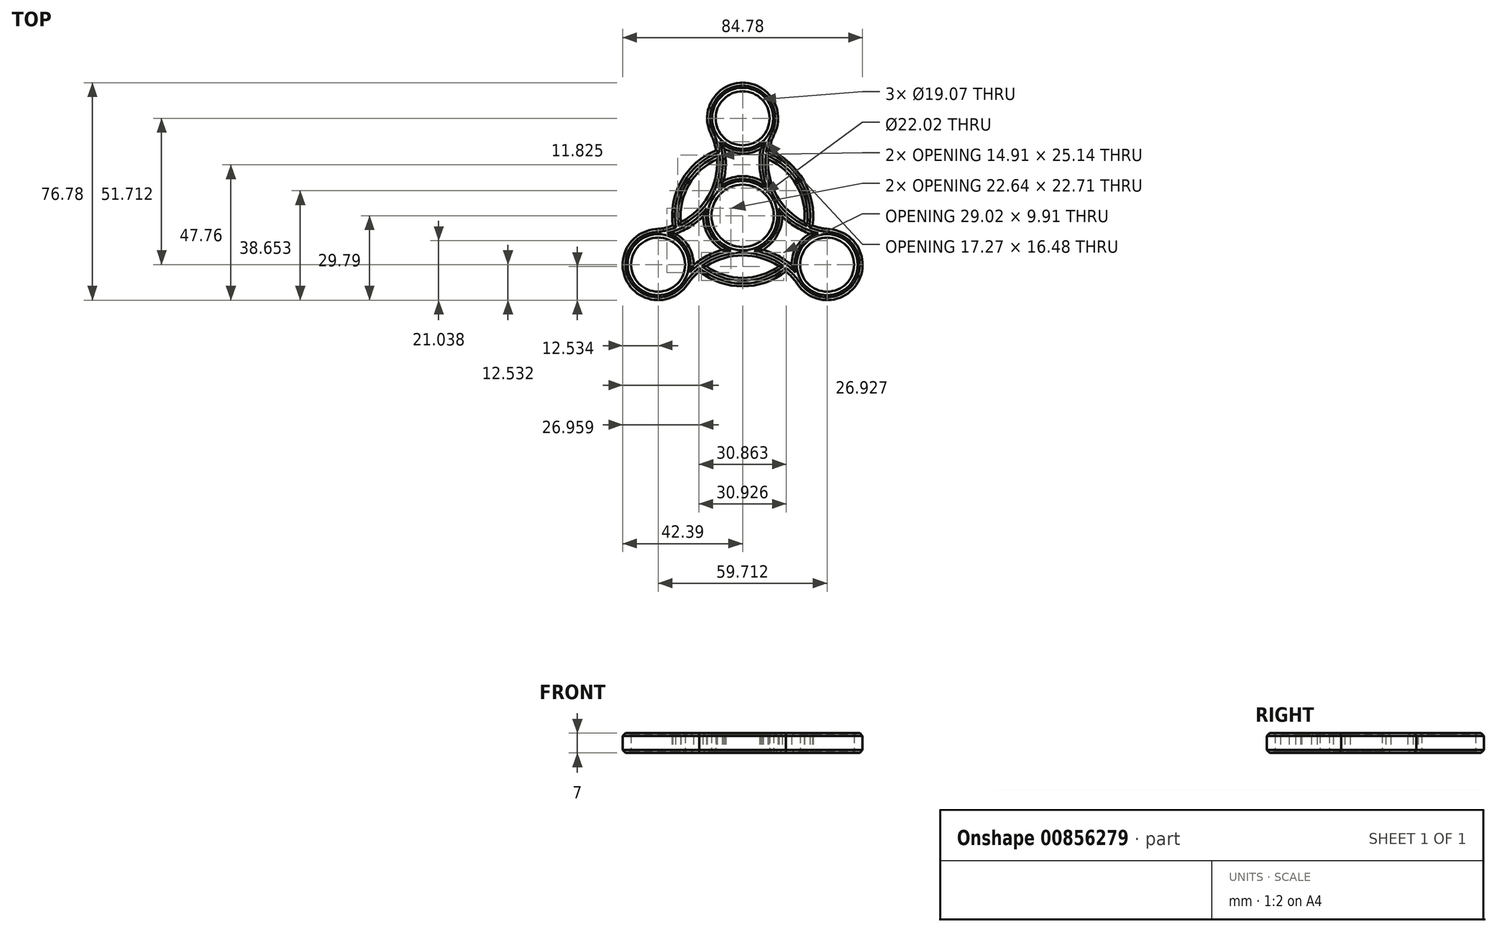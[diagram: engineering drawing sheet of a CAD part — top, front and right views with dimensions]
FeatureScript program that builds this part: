
annotation { "Feature Type Name" : "Feature", "Feature Type Description" : "" }
export const myFeature = defineFeature(function(context is Context, id is Id, definition is map)
    precondition{}
    {
        {
            var Q0;
            Q0=qCreatedBy(makeId("Top.planeOp"),FACE);
            var sketch = newSketch(context, id + "F0", { "sketchPlane" : qUnion([Q0])});
            skCircle(sketch, "E0", {"center": v(0, 0) * mm, "radius": 11.01 * mm});
            skCircle(sketch, "E1", {"center": v(0, 34.45) * mm, "radius": 9.54 * mm});
            skPoint(sketch, "E2", {"position": v(0, 43.99) * mm});
            skPoint(sketch, "E3", {"position": v(0, -11.01) * mm});
            skCircle(sketch, "E4.1.0", {"center": v(-29.86, -17.26) * mm, "radius": 9.54 * mm});
            skCircle(sketch, "E4.2.0", {"center": v(29.86, -17.26) * mm, "radius": 9.54 * mm});
            skPoint(sketch, "E4.center", {"position": v(0, -0.02) * mm});
            skArc(sketch, "E5", {"start": v(6.43, 23.7) * mm, "mid": v(5.99, 17.95) * mm, "end": v(6.8, 12.25) * mm});
            skArc(sketch, "E6", {"start": v(-23.75, -6.31) * mm, "mid": v(-18.55, -3.81) * mm, "end": v(-14, -0.25) * mm});
            skArc(sketch, "E7", {"start": v(17.32, -17.42) * mm, "mid": v(12.57, -14.17) * mm, "end": v(7.22, -12) * mm});
            skPoint(sketch, "E8", {"position": v(-21.98, -22.63) * mm});
            skPoint(sketch, "E9", {"position": v(-30.58, -7.75) * mm});
            skPoint(sketch, "E10", {"position": v(-8.6, 30.33) * mm});
            skPoint(sketch, "E11", {"position": v(8.6, 30.33) * mm});
            skPoint(sketch, "E12", {"position": v(30.58, -7.75) * mm});
            skPoint(sketch, "E13", {"position": v(21.98, -22.63) * mm});
            skPoint(sketch, "E14", {"position": v(-39.4, -17.26) * mm});
            skArc(sketch, "E15.0", {"start": v(-30.81, -4.76) * mm, "mid": v(-27.7, -4.31) * mm, "end": v(-24.68, -3.46) * mm});
            skArc(sketch, "E16.0", {"start": v(11.3, 29.03) * mm, "mid": v(10.14, 26.13) * mm, "end": v(9.37, 23.1) * mm});
            skArc(sketch, "E17.0", {"start": v(19.5, -24.32) * mm, "mid": v(17.56, -21.85) * mm, "end": v(15.32, -19.66) * mm});
            skArc(sketch, "E18.0", {"start": v(-17.32, -17.42) * mm, "mid": v(-19, -10.98) * mm, "end": v(-23.75, -6.31) * mm});
            skLineSegment(sketch, "E19.0", {"start": v(0, 46.99) * mm, "end": v(0, 46.99) * mm});
            skArc(sketch, "E20.0", {"start": v(23.75, -6.31) * mm, "mid": v(19, -10.98) * mm, "end": v(17.32, -17.42) * mm});
            skArc(sketch, "E21.0", {"start": v(6.8, 12.25) * mm, "mid": v(0, 14.01) * mm, "end": v(-6.8, 12.25) * mm});
            skArc(sketch, "E22.trimOffspring", {"start": v(0, 46.99) * mm, "mid": v(-10.6, 41.13) * mm, "end": v(-11.3, 29.03) * mm});
            skArc(sketch, "E23.trimOffspring", {"start": v(-6.43, 23.7) * mm, "mid": v(0, 21.92) * mm, "end": v(6.43, 23.7) * mm});
            skArc(sketch, "E24.trimOffspring", {"start": v(11.3, 29.03) * mm, "mid": v(11.3, 29.04) * mm, "end": v(11.3, 29.05) * mm});
            skArc(sketch, "E25.trimOffspring", {"start": v(30.4, -29.78) * mm, "mid": v(42.39, -17.46) * mm, "end": v(30.81, -4.76) * mm});
            skLineSegment(sketch, "E26.trimOffspring", {"start": v(30.4, -29.78) * mm, "end": v(30.4, -29.78) * mm});
            skArc(sketch, "E27.trimOffspring", {"start": v(19.5, -24.32) * mm, "mid": v(24.24, -28.46) * mm, "end": v(30.4, -29.78) * mm});
            skArc(sketch, "E28.trimOffspring", {"start": v(7.22, -12) * mm, "mid": v(12.13, -7) * mm, "end": v(14, -0.25) * mm});
            skArc(sketch, "E29.trimOffspring", {"start": v(-30.81, -4.76) * mm, "mid": v(-39.05, -8.74) * mm, "end": v(-42.4, -17.26) * mm});
            skArc(sketch, "E30.trimOffspring", {"start": v(-42.4, -17.26) * mm, "mid": v(-40.71, -23.53) * mm, "end": v(-36.12, -28.11) * mm});
            skArc(sketch, "E31.trimOffspring", {"start": v(-36.12, -28.11) * mm, "mid": v(-27.07, -29.48) * mm, "end": v(-19.5, -24.32) * mm});
            skArc(sketch, "E32.trimOffspring", {"start": v(-14, -0.25) * mm, "mid": v(-12.13, -7) * mm, "end": v(-7.22, -12) * mm});
            skArc(sketch, "E33.trimOffspring", {"start": v(-6.8, 12.25) * mm, "mid": v(-5.99, 17.95) * mm, "end": v(-6.43, 23.7) * mm});
            skArc(sketch, "E34.trimOffspring", {"start": v(14, -0.25) * mm, "mid": v(18.55, -3.81) * mm, "end": v(23.75, -6.31) * mm});
            skArc(sketch, "E35.trimOffspring", {"start": v(-7.22, -12) * mm, "mid": v(-12.57, -14.17) * mm, "end": v(-17.32, -17.42) * mm});
            skArc(sketch, "E36.trimOffspring", {"start": v(-11.3, 29.05) * mm, "mid": v(-11.3, 29.04) * mm, "end": v(-11.3, 29.03) * mm});
            skArc(sketch, "E37.trimOffspring", {"start": v(11.3, 29.03) * mm, "mid": v(10.6, 41.13) * mm, "end": v(0, 46.99) * mm});
            skArc(sketch, "E38", {"start": v(-9, 19.99) * mm, "mid": v(-18.99, 10.95) * mm, "end": v(-21.8, -2.21) * mm});
            skArc(sketch, "E39.0", {"start": v(-15.32, -19.66) * mm, "mid": v(0, -24.92) * mm, "end": v(15.32, -19.66) * mm});
            skArc(sketch, "E40.trimOffspring", {"start": v(-12.8, -17.79) * mm, "mid": v(0, -21.92) * mm, "end": v(12.8, -17.79) * mm});
            skArc(sketch, "E41.trimOffspring", {"start": v(24.68, -3.46) * mm, "mid": v(21.59, 12.45) * mm, "end": v(9.37, 23.1) * mm});
            skArc(sketch, "E42.trimOffspring", {"start": v(21.8, -2.21) * mm, "mid": v(18.99, 10.95) * mm, "end": v(9, 19.99) * mm});
            skArc(sketch, "E43.trimOffspring", {"start": v(-9.37, 23.1) * mm, "mid": v(-21.59, 12.45) * mm, "end": v(-24.68, -3.46) * mm});
            skArc(sketch, "E44.trimOffspring", {"start": v(9, 19.99) * mm, "mid": v(12.14, 7) * mm, "end": v(21.8, -2.21) * mm});
            skArc(sketch, "E45.trimOffspring", {"start": v(-9.37, 23.1) * mm, "mid": v(-10.14, 26.13) * mm, "end": v(-11.3, 29.03) * mm});
            skArc(sketch, "E46.trimOffspring", {"start": v(-21.8, -2.21) * mm, "mid": v(-12.14, 7) * mm, "end": v(-9, 19.99) * mm});
            skArc(sketch, "E47.trimOffspring", {"start": v(-15.32, -19.66) * mm, "mid": v(-17.56, -21.85) * mm, "end": v(-19.5, -24.32) * mm});
            skArc(sketch, "E48.trimOffspring", {"start": v(12.8, -17.79) * mm, "mid": v(0, -14.01) * mm, "end": v(-12.8, -17.79) * mm});
            skArc(sketch, "E49.trimOffspring", {"start": v(24.68, -3.46) * mm, "mid": v(27.7, -4.31) * mm, "end": v(30.81, -4.76) * mm});
            skSolve(sketch);
        }
        {
            var Q0;
            Q0=makeQuery(id+"F0.imprint","IMPRINT",FACE,{"disambiguationData":[TD([[makeQuery(id+"F0.imprint","IMPRINT",EDGE,{"derivedFrom":sQuery(id+"F0.wireOp",EDGE,"E0")}),-1.0]])]});
            extrude(context, id + "F1", {"entities" : qUnion([Q0]), "depth" : 7 * mm, "offsetDistance" : 25 * mm});
        }
        {
            var Q0;
            Q0=makeQuery(id+"F1.opExtrude","CAP_EDGE",EDGE,{"disambiguationData":[OSD([sQuery(id+"F0.wireOp",EDGE,"E4.2.0")])],"isStart":false});
            var Q1;
            Q1=makeQuery(id+"F1.opExtrude","CAP_EDGE",EDGE,{"disambiguationData":[OSD([sQuery(id+"F0.wireOp",EDGE,"E0")])],"isStart":false});
            var Q2;
            Q2=makeQuery(id+"F1.opExtrude","CAP_EDGE",EDGE,{"disambiguationData":[OSD([sQuery(id+"F0.wireOp",EDGE,"E1")])],"isStart":false});
            var Q3;
            Q3=makeQuery(id+"F1.opExtrude","CAP_EDGE",EDGE,{"disambiguationData":[OSD([sQuery(id+"F0.wireOp",EDGE,"E4.1.0")])],"isStart":false});
            var Q4;
            Q4=makeQuery(id+"F1.opExtrude","CAP_EDGE",EDGE,{"disambiguationData":[OSD([sQuery(id+"F0.wireOp",EDGE,"E4.2.0")])],"isStart":true});
            var Q5;
            Q5=makeQuery(id+"F1.opExtrude","CAP_EDGE",EDGE,{"disambiguationData":[OSD([sQuery(id+"F0.wireOp",EDGE,"E0")])],"isStart":true});
            var Q6;
            Q6=makeQuery(id+"F1.opExtrude","CAP_EDGE",EDGE,{"disambiguationData":[OSD([sQuery(id+"F0.wireOp",EDGE,"E1")])],"isStart":true});
            var Q7;
            Q7=makeQuery(id+"F1.opExtrude","CAP_EDGE",EDGE,{"disambiguationData":[OSD([sQuery(id+"F0.wireOp",EDGE,"E4.1.0")])],"isStart":true});
            chamfer(context, id + "F2", {"entities" : qUnion([Q0, Q1, Q2, Q3, Q4, Q5, Q6, Q7]), "width" : .25 * mm, "tangentPropagation" : true});
        }
        {
            var Q0;
            Q0=makeQuery(id+"F1.opExtrude","CAP_FACE",FACE,{"disambiguationData":[OSD([sQuery(id+"F0.wireOp",EDGE,"E0"),sQuery(id+"F0.wireOp",EDGE,"E1"),sQuery(id+"F0.wireOp",EDGE,"E4.1.0"),sQuery(id+"F0.wireOp",EDGE,"E4.2.0"),sQuery(id+"F0.wireOp",EDGE,"E5"),sQuery(id+"F0.wireOp",EDGE,"E6"),sQuery(id+"F0.wireOp",EDGE,"E7"),sQuery(id+"F0.wireOp",EDGE,"E15.0"),sQuery(id+"F0.wireOp",EDGE,"E16.0"),sQuery(id+"F0.wireOp",EDGE,"E17.0"),sQuery(id+"F0.wireOp",EDGE,"E18.0"),sQuery(id+"F0.wireOp",EDGE,"E20.0"),sQuery(id+"F0.wireOp",EDGE,"E21.0"),sQuery(id+"F0.wireOp",EDGE,"E22.trimOffspring"),sQuery(id+"F0.wireOp",EDGE,"E23.trimOffspring"),sQuery(id+"F0.wireOp",EDGE,"E24.trimOffspring"),sQuery(id+"F0.wireOp",EDGE,"E25.trimOffspring"),sQuery(id+"F0.wireOp",EDGE,"E27.trimOffspring"),sQuery(id+"F0.wireOp",EDGE,"E28.trimOffspring"),sQuery(id+"F0.wireOp",EDGE,"E29.trimOffspring"),sQuery(id+"F0.wireOp",EDGE,"E30.trimOffspring"),sQuery(id+"F0.wireOp",EDGE,"E31.trimOffspring"),sQuery(id+"F0.wireOp",EDGE,"E32.trimOffspring"),sQuery(id+"F0.wireOp",EDGE,"E33.trimOffspring"),sQuery(id+"F0.wireOp",EDGE,"E34.trimOffspring"),sQuery(id+"F0.wireOp",EDGE,"E35.trimOffspring"),sQuery(id+"F0.wireOp",EDGE,"CgF4OjDu-Xdq8-fYZo-l3O5-qwOTqDgyWiT8"),sQuery(id+"F0.wireOp",EDGE,"6862918b-1996-42d1-bb6a-92602a5ad6c9.0"),sQuery(id+"F0.wireOp",EDGE,"7e4e6287-273a-4d6e-a10a-42c86479f406.trimOffspring"),sQuery(id+"F0.wireOp",EDGE,"3e47e465-4781-4be7-9b47-1e3262841607.trimOffspring"),sQuery(id+"F0.wireOp",EDGE,"8596600d-4f88-4a93-9153-f14e8bb333e8.trimOffspring"),sQuery(id+"F0.wireOp",EDGE,"e53d3b50-5b82-4c0a-a50f-0517d6b8ebd0.trimOffspring"),sQuery(id+"F0.wireOp",EDGE,"E36.trimOffspring"),sQuery(id+"F0.wireOp",EDGE,"E37.trimOffspring")])],"isStart":false});
            var Q1;
            Q1=makeQuery(id+"F1.opExtrude","CAP_FACE",FACE,{"disambiguationData":[OSD([sQuery(id+"F0.wireOp",EDGE,"E0"),sQuery(id+"F0.wireOp",EDGE,"E1"),sQuery(id+"F0.wireOp",EDGE,"E4.1.0"),sQuery(id+"F0.wireOp",EDGE,"E4.2.0"),sQuery(id+"F0.wireOp",EDGE,"E5"),sQuery(id+"F0.wireOp",EDGE,"E6"),sQuery(id+"F0.wireOp",EDGE,"E7"),sQuery(id+"F0.wireOp",EDGE,"E15.0"),sQuery(id+"F0.wireOp",EDGE,"E16.0"),sQuery(id+"F0.wireOp",EDGE,"E17.0"),sQuery(id+"F0.wireOp",EDGE,"E18.0"),sQuery(id+"F0.wireOp",EDGE,"E20.0"),sQuery(id+"F0.wireOp",EDGE,"E21.0"),sQuery(id+"F0.wireOp",EDGE,"E22.trimOffspring"),sQuery(id+"F0.wireOp",EDGE,"E23.trimOffspring"),sQuery(id+"F0.wireOp",EDGE,"E24.trimOffspring"),sQuery(id+"F0.wireOp",EDGE,"E25.trimOffspring"),sQuery(id+"F0.wireOp",EDGE,"E27.trimOffspring"),sQuery(id+"F0.wireOp",EDGE,"E28.trimOffspring"),sQuery(id+"F0.wireOp",EDGE,"E29.trimOffspring"),sQuery(id+"F0.wireOp",EDGE,"E30.trimOffspring"),sQuery(id+"F0.wireOp",EDGE,"E31.trimOffspring"),sQuery(id+"F0.wireOp",EDGE,"E32.trimOffspring"),sQuery(id+"F0.wireOp",EDGE,"E33.trimOffspring"),sQuery(id+"F0.wireOp",EDGE,"E34.trimOffspring"),sQuery(id+"F0.wireOp",EDGE,"E35.trimOffspring"),sQuery(id+"F0.wireOp",EDGE,"CgF4OjDu-Xdq8-fYZo-l3O5-qwOTqDgyWiT8"),sQuery(id+"F0.wireOp",EDGE,"6862918b-1996-42d1-bb6a-92602a5ad6c9.0"),sQuery(id+"F0.wireOp",EDGE,"7e4e6287-273a-4d6e-a10a-42c86479f406.trimOffspring"),sQuery(id+"F0.wireOp",EDGE,"3e47e465-4781-4be7-9b47-1e3262841607.trimOffspring"),sQuery(id+"F0.wireOp",EDGE,"8596600d-4f88-4a93-9153-f14e8bb333e8.trimOffspring"),sQuery(id+"F0.wireOp",EDGE,"e53d3b50-5b82-4c0a-a50f-0517d6b8ebd0.trimOffspring"),sQuery(id+"F0.wireOp",EDGE,"E36.trimOffspring"),sQuery(id+"F0.wireOp",EDGE,"E37.trimOffspring")])],"isStart":true});
            chamfer(context, id + "F3", {"entities" : qUnion([Q0, Q1]), "width" : 1 * mm, "tangentPropagation" : true});
        }
    });
